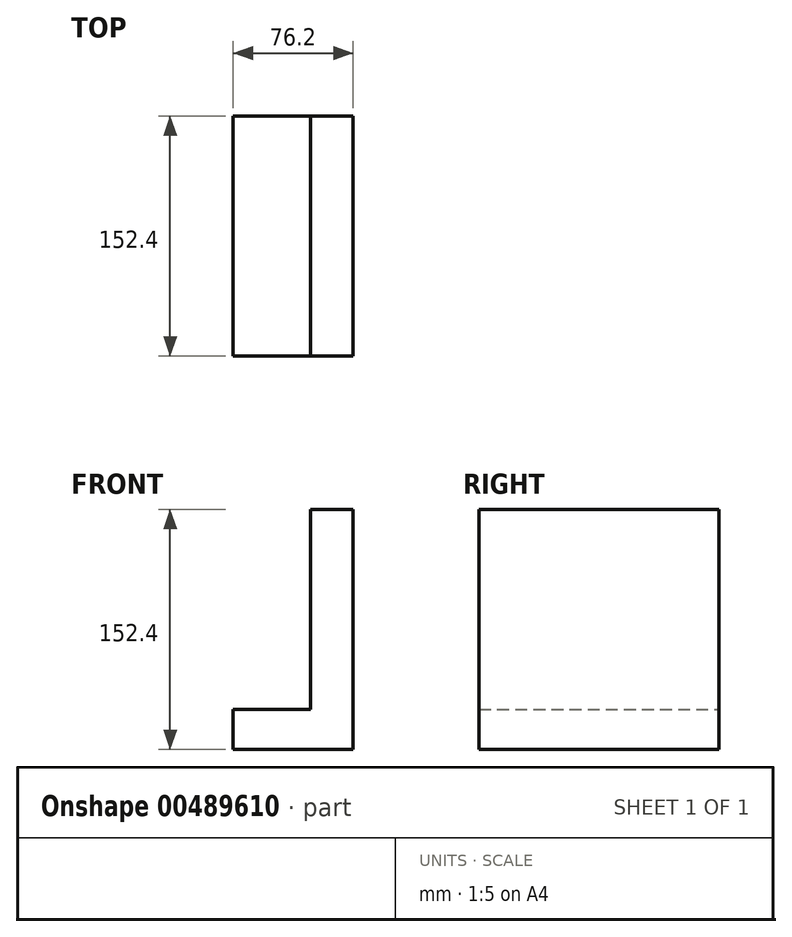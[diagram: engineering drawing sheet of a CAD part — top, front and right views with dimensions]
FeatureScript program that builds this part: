
annotation { "Feature Type Name" : "Feature", "Feature Type Description" : "" }
export const myFeature = defineFeature(function(context is Context, id is Id, definition is map)
    precondition{}
    {
        {
            var Q0;
            Q0=qCreatedBy(makeId("Front.planeOp"),FACE);
            var sketch = newSketch(context, id + "F0", { "sketchPlane" : qUnion([Q0])});
            skLineSegment(sketch, "E0", {"start": v(0, 152.4) * mm, "end": v(-27.21, 152.4) * mm});
            skLineSegment(sketch, "E1", {"start": v(-27.21, 152.4) * mm, "end": v(-27.21, 25.4) * mm});
            skLineSegment(sketch, "E2", {"start": v(-27.21, 25.4) * mm, "end": v(-76.2, 25.4) * mm});
            skLineSegment(sketch, "E3", {"start": v(-76.2, 25.4) * mm, "end": v(-76.2, 0) * mm});
            skLineSegment(sketch, "E4", {"start": v(-76.2, 0) * mm, "end": v(0, 0) * mm});
            skLineSegment(sketch, "E5", {"start": v(0, 0) * mm, "end": v(0, 152.4) * mm});
            skSolve(sketch);
        }
        {
            var Q0;
            Q0 = qSketchRegion(id + "F0", true);
            extrude(context, id + "F1", {"entities" : qUnion([Q0]), "depth" : 152.4 * mm});
        }
    });
